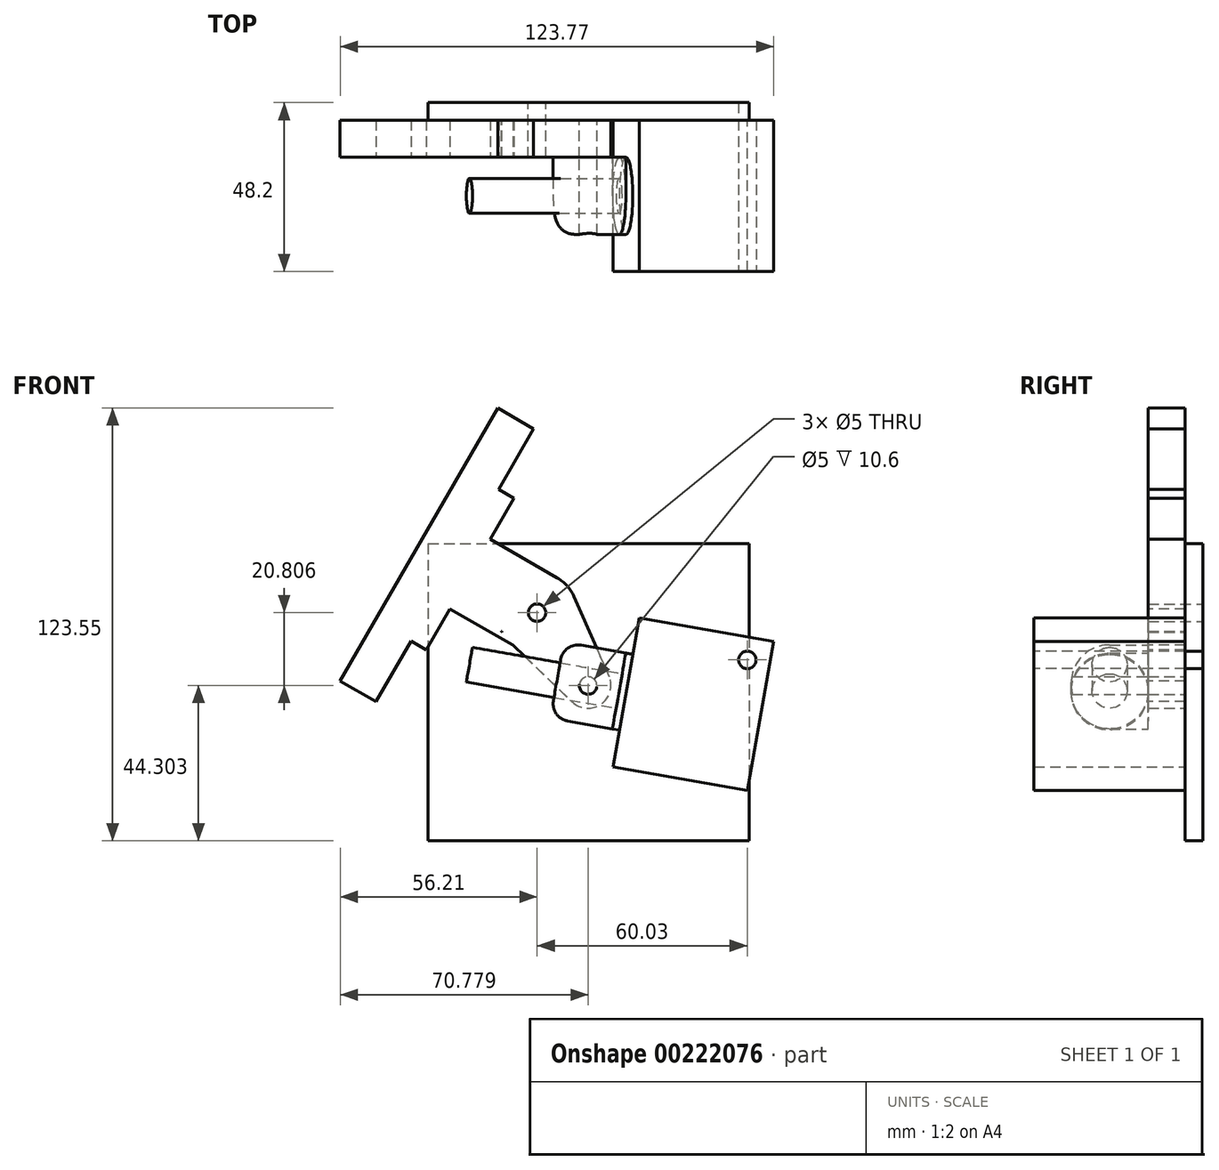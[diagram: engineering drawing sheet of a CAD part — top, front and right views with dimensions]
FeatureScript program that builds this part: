
annotation { "Feature Type Name" : "Feature", "Feature Type Description" : "" }
export const myFeature = defineFeature(function(context is Context, id is Id, definition is map)
    precondition{}
    {
        {
            var Q0;
            Q0=qCreatedBy(makeId("Front.planeOp"),FACE);
            var sketch = newSketch(context, id + "F0", { "sketchPlane" : qUnion([Q0])});
            skArc(sketch, "E0", {"start": v(10.53, 4.61) * mm, "mid": v(-6.6, 9.42) * mm, "end": v(-7.94, -8.32) * mm});
            skCircle(sketch, "E1", {"center": v(0, 0) * mm, "radius": 2.5 * mm});
            skLineSegment(sketch, "E2", {"start": v(-23.42, 12.9) * mm, "end": v(20.76, 12.9) * mm, "construction": true});
            skCircle(sketch, "E3", {"center": v(0, 0) * mm, "radius": 25.4 * mm, "construction": true});
            skLineSegment(sketch, "E4", {"start": v(0, 0) * mm, "end": v(14.57, -20.8) * mm, "construction": true});
            skLineSegment(sketch, "E5", {"start": v(14.57, -20.8) * mm, "end": v(25.4, -22.72) * mm, "construction": true});
            skLineSegment(sketch, "E6", {"start": v(25.4, -22.72) * mm, "end": v(27.31, -11.88) * mm, "construction": true});
            skLineSegment(sketch, "E7", {"start": v(23.5, -33.55) * mm, "end": v(25.4, -22.72) * mm, "construction": true});
            skLineSegment(sketch, "E8", {"start": v(25.4, -22.72) * mm, "end": v(29.15, -1.44) * mm});
            skLineSegment(sketch, "E9", {"start": v(25.4, -22.72) * mm, "end": v(21.65, -43.99) * mm});
            skLineSegment(sketch, "E10", {"start": v(21.65, -43.99) * mm, "end": v(60.06, -50.76) * mm});
            skLineSegment(sketch, "E11", {"start": v(29.15, -1.44) * mm, "end": v(67.56, -8.22) * mm});
            skLineSegment(sketch, "E12", {"start": v(67.56, -8.22) * mm, "end": v(60.06, -50.76) * mm});
            skArc(sketch, "E13", {"start": v(10.08, -25.5) * mm, "mid": v(18.3, -26.13) * mm, "end": v(20.52, -18.2) * mm});
            skLineSegment(sketch, "E14", {"start": v(-7.94, -8.32) * mm, "end": v(10.08, -25.5) * mm});
            skLineSegment(sketch, "E15", {"start": v(10.53, 4.61) * mm, "end": v(20.52, -18.2) * mm});
            skCircle(sketch, "E16", {"center": v(14.57, -20.8) * mm, "radius": 2.5 * mm});
            skCircle(sketch, "E17", {"center": v(-20.8, -14.57) * mm, "radius": 6.5 * mm});
            skPoint(sketch, "E18.startSnap0", {"position": v(-8.16, -9.73) * mm});
            skLineSegment(sketch, "E19", {"start": v(-11.94, -16.13) * mm, "end": v(-13.85, -26.96) * mm});
            skLineSegment(sketch, "E20", {"start": v(-13.85, -26.96) * mm, "end": v(-10.03, -5.3) * mm});
            skLineSegment(sketch, "E21", {"start": v(-10.03, -5.3) * mm, "end": v(-22.84, -3.04) * mm});
            skLineSegment(sketch, "E22", {"start": v(-28.63, -7.1) * mm, "end": v(-30.71, -18.91) * mm});
            skLineSegment(sketch, "E23", {"start": v(-26.66, -24.7) * mm, "end": v(-13.85, -26.96) * mm});
            skPoint(sketch, "E24.visualSharp", {"position": v(-27.76, -2.17) * mm});
            skArc(sketch, "E24.filletArc", {"start": v(-22.84, -3.04) * mm, "mid": v(-26.57, -3.87) * mm, "end": v(-28.63, -7.1) * mm});
            skPoint(sketch, "E25.visualSharp", {"position": v(-31.58, -23.84) * mm});
            skArc(sketch, "E25.filletArc", {"start": v(-30.71, -18.91) * mm, "mid": v(-29.88, -22.65) * mm, "end": v(-26.66, -24.7) * mm});
            skLineSegment(sketch, "E26", {"start": v(-27.76, 12.9) * mm, "end": v(-49.26, -46.16) * mm, "construction": true});
            skLineSegment(sketch, "E27", {"start": v(25.4, -22.72) * mm, "end": v(-20.8, -14.57) * mm});
            skLineSegment(sketch, "E28", {"start": v(-20.8, -14.57) * mm, "end": v(0, 0) * mm, "construction": true});
            skLineSegment(sketch, "E29", {"start": v(18.09, 12.9) * mm, "end": v(75.65, -20.33) * mm, "construction": true});
            skLineSegment(sketch, "E30", {"start": v(44.61, -51.34) * mm, "end": v(-29.39, -51.34) * mm});
            skLineSegment(sketch, "E31", {"start": v(-29.39, -51.34) * mm, "end": v(-29.39, -67.34) * mm});
            skLineSegment(sketch, "E32", {"start": v(-29.39, -67.34) * mm, "end": v(44.61, -67.34) * mm});
            skLineSegment(sketch, "E33", {"start": v(44.61, -67.34) * mm, "end": v(44.61, -51.34) * mm});
            skCircle(sketch, "E34", {"center": v(0, -25.4) * mm, "radius": 9.5 * mm});
            skLineSegment(sketch, "E35", {"start": v(0, 0) * mm, "end": v(-23.38, 13.5) * mm});
            skLineSegment(sketch, "E36", {"start": v(-23.38, 13.5) * mm, "end": v(-45.88, -25.47) * mm});
            skLineSegment(sketch, "E37", {"start": v(-23.38, 13.5) * mm, "end": v(-20.88, 17.83) * mm});
            skLineSegment(sketch, "E38", {"start": v(-20.88, 17.83) * mm, "end": v(-31.27, 23.83) * mm});
            skLineSegment(sketch, "E39", {"start": v(-31.27, 23.83) * mm, "end": v(-56.27, -19.47) * mm});
            skLineSegment(sketch, "E40", {"start": v(-45.88, -25.47) * mm, "end": v(-56.27, -19.47) * mm});
            skSolve(sketch);
        }
        {
            var Q0;
            Q0=makeQuery(id+"F0.imprint","IMPRINT",FACE,{"disambiguationData":[TD([[makeQuery(id+"F0.imprint","IMPRINT",EDGE,{"derivedFrom":sQuery(id+"F0.wireOp",EDGE,"E0")}),1.0]])]});
            var Q1;
            {var subQ0=sQuery(id+"F0.wireOp",EDGE,"E21");var subQ1=sQuery(id+"F0.wireOp",EDGE,"E14");var subQ2=makeQuery(id+"F0.imprint","INTERSECT",VERTEX,{"derivedFrom":[subQ1,subQ0]});Q1=makeQuery(id+"F0.imprint","IMPRINT",FACE,{"disambiguationData":[TD([[makeQuery(id+"F0.imprint","IMPRINT",EDGE,{"disambiguationData":[TD([[subQ2,-1.0]])],"derivedFrom":subQ1}),1.0]])]});}
            var Q2;
            {var subQ1=sQuery(id+"F0.wireOp",EDGE,"E13");var subQ6=sQuery(id+"F0.wireOp",EDGE,"E14");var subQ7=makeQuery(id+"F0.imprint","INTERSECT",VERTEX,{"derivedFrom":[subQ1,subQ6]});Q2=makeQuery(id+"F0.imprint","IMPRINT",FACE,{"disambiguationData":[TD([[makeQuery(id+"F0.imprint","IMPRINT",EDGE,{"disambiguationData":[TD([[subQ7,-1.0]])],"derivedFrom":subQ1}),1.0]])]});}
            extrude(context, id + "F1", {"entities" : qUnion([Q0, Q1, Q2]), "depth" : 10.6 * mm, "offsetDistance" : 25 * mm});
        }
        {
            var Q0;
            Q0=makeQuery(id+"F0.imprint","IMPRINT",FACE,{"disambiguationData":[TD([[makeQuery(id+"F0.imprint","IMPRINT",EDGE,{"derivedFrom":sQuery(id+"F0.wireOp",EDGE,"E8")}),-1.0]])]});
            extrude(context, id + "F2", {"entities" : qUnion([Q0]), "depth" : 43.2 * mm, "offsetDistance" : 25 * mm});
        }
        {
            var Q0;
            Q0=makeQuery(id+"F2.opExtrude","SWEPT_FACE",FACE,{"disambiguationData":[OSD([sQuery(id+"F0.wireOp",EDGE,"E8"),sQuery(id+"F0.wireOp",EDGE,"E9")])]});
            var sketch = newSketch(context, id + "F3", { "sketchPlane" : qUnion([Q0])});
            skCircle(sketch, "E41", {"center": v(21.6, -17.96) * mm, "radius": 11 * mm});
            skPoint(sketch, "E41.centerSnap0", {"position": v(43.2, -17.96) * mm});
            skPoint(sketch, "E41.centerSnap1", {"position": v(21.6, 3.64) * mm});
            skSolve(sketch);
        }
        {
            var Q0;
            Q0=makeQuery(id+"F3.imprint","IMPRINT",FACE,{"disambiguationData":[TD([[makeQuery(id+"F3.imprint","IMPRINT",EDGE,{"derivedFrom":sQuery(id+"F3.wireOp",EDGE,"E41")}),1.0]])]});
            extrude(context, id + "F4", {"entities" : qUnion([Q0]), "operationType" : NewBodyOperationType.ADD, "depth" : 2 * mm, "offsetDistance" : 25 * mm});
        }
        {
            var Q0;
            Q0=makeQuery(id+"F4.opExtrude","CAP_FACE",FACE,{"disambiguationData":[OSD([sQuery(id+"F3.wireOp",EDGE,"E41")])],"isStart":false});
            var sketch = newSketch(context, id + "F5", { "sketchPlane" : qUnion([Q0])});
            skCircle(sketch, "E42.0", {"center": v(21.6, -17.96) * mm, "radius": 11 * mm});
            skCircle(sketch, "E43", {"center": v(21.6, -17.96) * mm, "radius": 5 * mm});
            skSolve(sketch);
        }
        {
            var Q0;
            Q0=makeQuery(id+"F5.imprint","IMPRINT",FACE,{"disambiguationData":[TD([[makeQuery(id+"F5.imprint","IMPRINT",EDGE,{"derivedFrom":sQuery(id+"F5.wireOp",EDGE,"E43")}),1.0]])]});
            extrude(context, id + "F6", {"entities" : qUnion([Q0]), "operationType" : NewBodyOperationType.ADD, "depth" : (45.4 - 2) * mm, "offsetDistance" : 25 * mm});
        }
        {
            var Q0;
            Q0=makeQuery(id+"F1.opExtrude","CAP_FACE",FACE,{"disambiguationData":[OSD([sQuery(id+"F0.wireOp",EDGE,"E0"),sQuery(id+"F0.wireOp",EDGE,"E1"),sQuery(id+"F0.wireOp",EDGE,"E13"),sQuery(id+"F0.wireOp",EDGE,"E14"),sQuery(id+"F0.wireOp",EDGE,"E15"),sQuery(id+"F0.wireOp",EDGE,"E16")])],"isStart":false});
            var sketch = newSketch(context, id + "F7", { "sketchPlane" : qUnion([Q0])});
            skCircle(sketch, "E44.0", {"center": v(14.57, -20.8) * mm, "radius": 2.5 * mm});
            skLineSegment(sketch, "E45.0", {"start": v(21.52, -33.2) * mm, "end": v(25.34, -11.54) * mm});
            skLineSegment(sketch, "E46", {"start": v(25.34, -11.54) * mm, "end": v(7.62, -8.41) * mm});
            skLineSegment(sketch, "E47", {"start": v(21.52, -33.2) * mm, "end": v(3.8, -30.08) * mm});
            skLineSegment(sketch, "E48", {"start": v(7.62, -8.41) * mm, "end": v(3.8, -30.08) * mm});
            skSolve(sketch);
        }
        {
            var Q0;
            {var subQ1=sQuery(id+"F7.wireOp",EDGE,"E47");Q0=makeQuery(id+"F7.imprint","IMPRINT",FACE,{"disambiguationData":[TD([[makeQuery(id+"F7.imprint","IMPRINT",EDGE,{"derivedFrom":subQ1}),-1.0]])]});}
            var Q1;
            Q1=makeQuery(id+"F7.imprint","IMPRINT",FACE,{"disambiguationData":[TD([[makeQuery(id+"F7.imprint","IMPRINT",EDGE,{"derivedFrom":sQuery(id+"F7.wireOp",EDGE,"E44.0")}),-1.0]])]});
            var Q2;
            {var subQ0=sQuery(id+"F7.wireOp",EDGE,"E46");var subQ1=sQuery(id+"F7.wireOp",EDGE,"E45.0");var subQ2=makeQuery(id+"F7.imprint","INTERSECT",VERTEX,{"derivedFrom":[subQ1,subQ0]});Q2=makeQuery(id+"F7.imprint","IMPRINT",FACE,{"disambiguationData":[TD([[makeQuery(id+"F7.imprint","IMPRINT",EDGE,{"disambiguationData":[TD([[subQ2,1.0]])],"derivedFrom":subQ1}),1.0]])]});}
            var Q3;
            {var subQ8=sQuery(id+"F0.wireOp",EDGE,"E13");var subQ9=makeQuery(id+"F1.opExtrude","CAP_EDGE",EDGE,{"disambiguationData":[OSD([subQ8])],"isStart":false});Q3=makeQuery(id+"F7.imprint","IMPRINT",FACE,{"disambiguationData":[TD([[makeQuery(id+"F7.imprint","IMPRINT",EDGE,{"derivedFrom":subQ9}),1.0]])]});}
            extrude(context, id + "F8", {"entities" : qUnion([Q0, Q1, Q2, Q3]), "depth" : 22 * mm, "offsetDistance" : 25 * mm});
        }
        {
            var Q0;
            Q0=makeQuery(id+"F8.opExtrude","CAP_EDGE",EDGE,{"disambiguationData":[OSD([sQuery(id+"F7.wireOp",EDGE,"E46")])],"isStart":false});
            var Q1;
            Q1=makeQuery(id+"F8.opExtrude","CAP_EDGE",EDGE,{"disambiguationData":[OSD([sQuery(id+"F7.wireOp",EDGE,"E47")])],"isStart":false});
            fillet(context, id + "F9", {"entities" : qUnion([Q0, Q1]), "radius" : 11 * mm, "tangentPropagation" : true, "allowEdgeOverflow" : false});
        }
        {
            var Q0;
            Q0=makeQuery(id+"F0.imprint","IMPRINT",FACE,{"disambiguationData":[TD([[makeQuery(id+"F0.imprint","IMPRINT",EDGE,{"derivedFrom":sQuery(id+"F0.wireOp",EDGE,"E0")}),1.0]])]});
            var sketch = newSketch(context, id + "F10", { "sketchPlane" : qUnion([Q0])});
            skLineSegment(sketch, "E49.bottom", {"start": v(-31.15, 19.66) * mm, "end": v(60.52, 19.66) * mm});
            skLineSegment(sketch, "E49.top", {"start": v(-31.15, -65.11) * mm, "end": v(60.52, -65.11) * mm});
            skLineSegment(sketch, "E49.left", {"start": v(-31.15, 19.66) * mm, "end": v(-31.15, -65.11) * mm});
            skLineSegment(sketch, "E49.right", {"start": v(60.52, 19.66) * mm, "end": v(60.52, -65.11) * mm});
            skSolve(sketch);
        }
        {
            var Q0;
            Q0=makeQuery(id+"F10.imprint","IMPRINT",FACE,{"disambiguationData":[TD([[makeQuery(id+"F10.imprint","IMPRINT",EDGE,{"derivedFrom":sQuery(id+"F10.wireOp",EDGE,"E49.bottom")}),-1.0]])]});
            var Q1;
            Q1=makeQuery(id+"F0.imprint","IMPRINT",FACE,{"disambiguationData":[TD([[makeQuery(id+"F0.imprint","IMPRINT",EDGE,{"derivedFrom":sQuery(id+"F0.wireOp",EDGE,"E0")}),1.0]])]});
            var Q2;
            Q2=makeQuery(id+"F0.imprint","IMPRINT",FACE,{"disambiguationData":[TD([[makeQuery(id+"F0.imprint","IMPRINT",EDGE,{"derivedFrom":sQuery(id+"F0.wireOp",EDGE,"E16")}),1.0]])]});
            extrude(context, id + "F11", {"entities" : qUnion([Q0, Q1, Q2]), "oppositeDirection" : true, "depth" : 5 * mm, "offsetDistance" : 25 * mm});
        }
        {
            var Q0;
            Q0=makeQuery(id+"F2.opExtrude","CAP_FACE",FACE,{"disambiguationData":[OSD([sQuery(id+"F0.wireOp",EDGE,"E8"),sQuery(id+"F0.wireOp",EDGE,"E9"),sQuery(id+"F0.wireOp",EDGE,"E10"),sQuery(id+"F0.wireOp",EDGE,"E11"),sQuery(id+"F0.wireOp",EDGE,"E12")])],"isStart":false});
            var sketch = newSketch(context, id + "F12", { "sketchPlane" : qUnion([Q0])});
            skCircle(sketch, "E50", {"center": v(60.03, -13.49) * mm, "radius": 6.5 * mm});
            skCircle(sketch, "E51", {"center": v(60.03, -13.49) * mm, "radius": 2.5 * mm});
            skSolve(sketch);
        }
        {
            var Q0;
            Q0=makeQuery(id+"F12.imprint","IMPRINT",FACE,{"disambiguationData":[TD([[makeQuery(id+"F12.imprint","IMPRINT",EDGE,{"derivedFrom":sQuery(id+"F12.wireOp",EDGE,"E51")}),1.0]])]});
            extrude(context, id + "F13", {"entities" : qUnion([Q0]), "operationType" : NewBodyOperationType.REMOVE, "oppositeDirection" : true, "depth" : 74.8 * mm, "offsetDistance" : 25 * mm});
        }
        {
            var Q0;
            Q0=makeQuery(id+"F1.opExtrude","CAP_FACE",FACE,{"disambiguationData":[OSD([sQuery(id+"F0.wireOp",EDGE,"E0"),sQuery(id+"F0.wireOp",EDGE,"E1"),sQuery(id+"F0.wireOp",EDGE,"E13"),sQuery(id+"F0.wireOp",EDGE,"E14"),sQuery(id+"F0.wireOp",EDGE,"E15"),sQuery(id+"F0.wireOp",EDGE,"E16")])],"isStart":false});
            var sketch = newSketch(context, id + "F14", { "sketchPlane" : qUnion([Q0])});
            skLineSegment(sketch, "E52", {"start": v(-24.91, 1.1) * mm, "end": v(-31.66, -10.59) * mm});
            skLineSegment(sketch, "E53", {"start": v(-31.66, -10.59) * mm, "end": v(-36, -8.09) * mm});
            skLineSegment(sketch, "E54", {"start": v(-36, -8.09) * mm, "end": v(-17.74, 23.52) * mm});
            skLineSegment(sketch, "E55", {"start": v(-13.41, 21.02) * mm, "end": v(5.75, 9.96) * mm});
            skArc(sketch, "E56.0", {"start": v(10.53, 4.61) * mm, "mid": v(-6.6, 9.42) * mm, "end": v(-7.94, -8.32) * mm});
            skLineSegment(sketch, "E57", {"start": v(-24.91, 1.1) * mm, "end": v(-6.94, -9.27) * mm});
            skLineSegment(sketch, "E58.0", {"start": v(-20.18, -19.76) * mm, "end": v(-18.44, -9.9) * mm});
            skLineSegment(sketch, "E59", {"start": v(-13.41, 21.02) * mm, "end": v(-6.66, 32.72) * mm});
            skLineSegment(sketch, "E60", {"start": v(-17.74, 23.52) * mm, "end": v(-11, 35.22) * mm});
            skLineSegment(sketch, "E61", {"start": v(-11, 35.22) * mm, "end": v(-6.66, 32.72) * mm});
            skLineSegment(sketch, "E62", {"start": v(-1, 52.54) * mm, "end": v(-46, -25.4) * mm});
            skLineSegment(sketch, "E63", {"start": v(-46, -25.4) * mm, "end": v(-56.21, -19.5) * mm});
            skLineSegment(sketch, "E64", {"start": v(-56.21, -19.5) * mm, "end": v(-11.21, 58.44) * mm});
            skLineSegment(sketch, "E65", {"start": v(-1, 52.54) * mm, "end": v(-11.21, 58.44) * mm});
            skLineSegment(sketch, "E66", {"start": v(0, 0) * mm, "end": v(-23.5, 13.56) * mm});
            skLineSegment(sketch, "E67", {"start": v(-36, -8.09) * mm, "end": v(-41.62, -4.84) * mm});
            skLineSegment(sketch, "E68", {"start": v(-41.62, -4.84) * mm, "end": v(-16.62, 38.47) * mm});
            skLineSegment(sketch, "E69", {"start": v(-11, 35.22) * mm, "end": v(-16.62, 38.47) * mm});
            skLineSegment(sketch, "E70.0", {"start": v(-7.94, -8.32) * mm, "end": v(-7.94, -8.32) * mm});
            skLineSegment(sketch, "E71.bottom", {"start": v(44.66, -52.76) * mm, "end": v(1.46, -52.76) * mm, "construction": true});
            skLineSegment(sketch, "E71.top", {"start": v(44.66, 0.24) * mm, "end": v(1.46, 0.24) * mm, "construction": true});
            skLineSegment(sketch, "E71.left", {"start": v(44.66, -52.76) * mm, "end": v(44.66, 0.24) * mm, "construction": true});
            skLineSegment(sketch, "E71.right", {"start": v(1.46, -52.76) * mm, "end": v(1.46, 0.24) * mm, "construction": true});
            skPoint(sketch, "E71.middle", {"position": v(23.06, -26.26) * mm});
            skLineSegment(sketch, "E72.bottom", {"start": v(62.06, -52.76) * mm, "end": v(-15.94, -52.76) * mm, "construction": true});
            skLineSegment(sketch, "E72.top", {"start": v(62.06, -70.76) * mm, "end": v(-15.94, -70.76) * mm, "construction": true});
            skLineSegment(sketch, "E72.left", {"start": v(62.06, -52.76) * mm, "end": v(62.06, -70.76) * mm, "construction": true});
            skLineSegment(sketch, "E72.right", {"start": v(-15.94, -52.76) * mm, "end": v(-15.94, -70.76) * mm, "construction": true});
            skPoint(sketch, "E72.middle", {"position": v(23.06, -61.76) * mm});
            skPoint(sketch, "E72.middle.positionSnap0", {"position": v(23.06, -52.76) * mm});
            skPoint(sketch, "E72.cornerSnap0", {"position": v(23.06, -52.76) * mm});
            skPoint(sketch, "E72.centerSnap0", {"position": v(23.06, -52.76) * mm});
            skCircle(sketch, "E73", {"center": v(0, 0) * mm, "radius": 24.94 * mm, "construction": true});
            skLineSegment(sketch, "E74", {"start": v(-25.18, -14.9) * mm, "end": v(-25.18, -49.9) * mm});
            skLineSegment(sketch, "E75", {"start": v(-24.94, 0) * mm, "end": v(-25.18, -14.9) * mm});
            skLineSegment(sketch, "E76.0", {"start": v(29.15, -1.44) * mm, "end": v(67.56, -8.22) * mm});
            skLineSegment(sketch, "E77", {"start": v(24.94, 0) * mm, "end": v(71.56, -8.22) * mm});
            skLineSegment(sketch, "E78", {"start": v(71.56, -8.22) * mm, "end": v(71.56, -49.9) * mm});
            skPoint(sketch, "E79.start.orphan", {"position": v(62.06, -47.73) * mm});
            skLineSegment(sketch, "E80.0", {"start": v(21.65, -43.99) * mm, "end": v(60.06, -50.76) * mm});
            skSolve(sketch);
        }
        {
            var Q0;
            Q0=makeQuery(id+"F14.imprint","IMPRINT",FACE,{"disambiguationData":[TD([[makeQuery(id+"F14.imprint","IMPRINT",EDGE,{"derivedFrom":sQuery(id+"F14.wireOp",EDGE,"E52")}),-1.0]])]});
            var Q1;
            {var subQ2=sQuery(id+"F14.wireOp",EDGE,"E55");Q1=makeQuery(id+"F14.imprint","IMPRINT",FACE,{"disambiguationData":[TD([[makeQuery(id+"F14.imprint","IMPRINT",EDGE,{"derivedFrom":subQ2}),-1.0]])]});}
            var Q2;
            {var subQ0=sQuery(id+"F14.wireOp",EDGE,"E67");Q2=makeQuery(id+"F14.imprint","IMPRINT",FACE,{"disambiguationData":[TD([[makeQuery(id+"F14.imprint","IMPRINT",EDGE,{"derivedFrom":subQ0}),-1.0]])]});}
            var Q3;
            {var subQ0=sQuery(id+"F14.wireOp",EDGE,"E63");Q3=makeQuery(id+"F14.imprint","IMPRINT",FACE,{"disambiguationData":[TD([[makeQuery(id+"F14.imprint","IMPRINT",EDGE,{"derivedFrom":subQ0}),-1.0]])]});}
            extrude(context, id + "F15", {"entities" : qUnion([Q0, Q1, Q2, Q3]), "operationType" : NewBodyOperationType.ADD, "oppositeDirection" : true, "depth" : 10.6 * mm, "offsetDistance" : 25 * mm});
        }
        {
            var Q0;
            Q0=makeQuery(id+"F9.opFillet","BLEND_EDGE",EDGE,{"blendedFrom":[makeQuery(id+"F8.opExtrude","CAP_EDGE",EDGE,{"disambiguationData":[OSD([sQuery(id+"F7.wireOp",EDGE,"E46")])],"isStart":false}),makeQuery(id+"F8.opExtrude","SWEPT_FACE",FACE,{"disambiguationData":[OSD([sQuery(id+"F7.wireOp",EDGE,"E48")])]})],"blendedInto":[makeQuery(id+"F8.opExtrude","SWEPT_FACE",FACE,{"disambiguationData":[OSD([sQuery(id+"F7.wireOp",EDGE,"E48")])]})]});
            fillet(context, id + "F16", {"entities" : qUnion([Q0]), "radius" : 5 * mm, "tangentPropagation" : true, "allowEdgeOverflow" : false});
        }
    });
